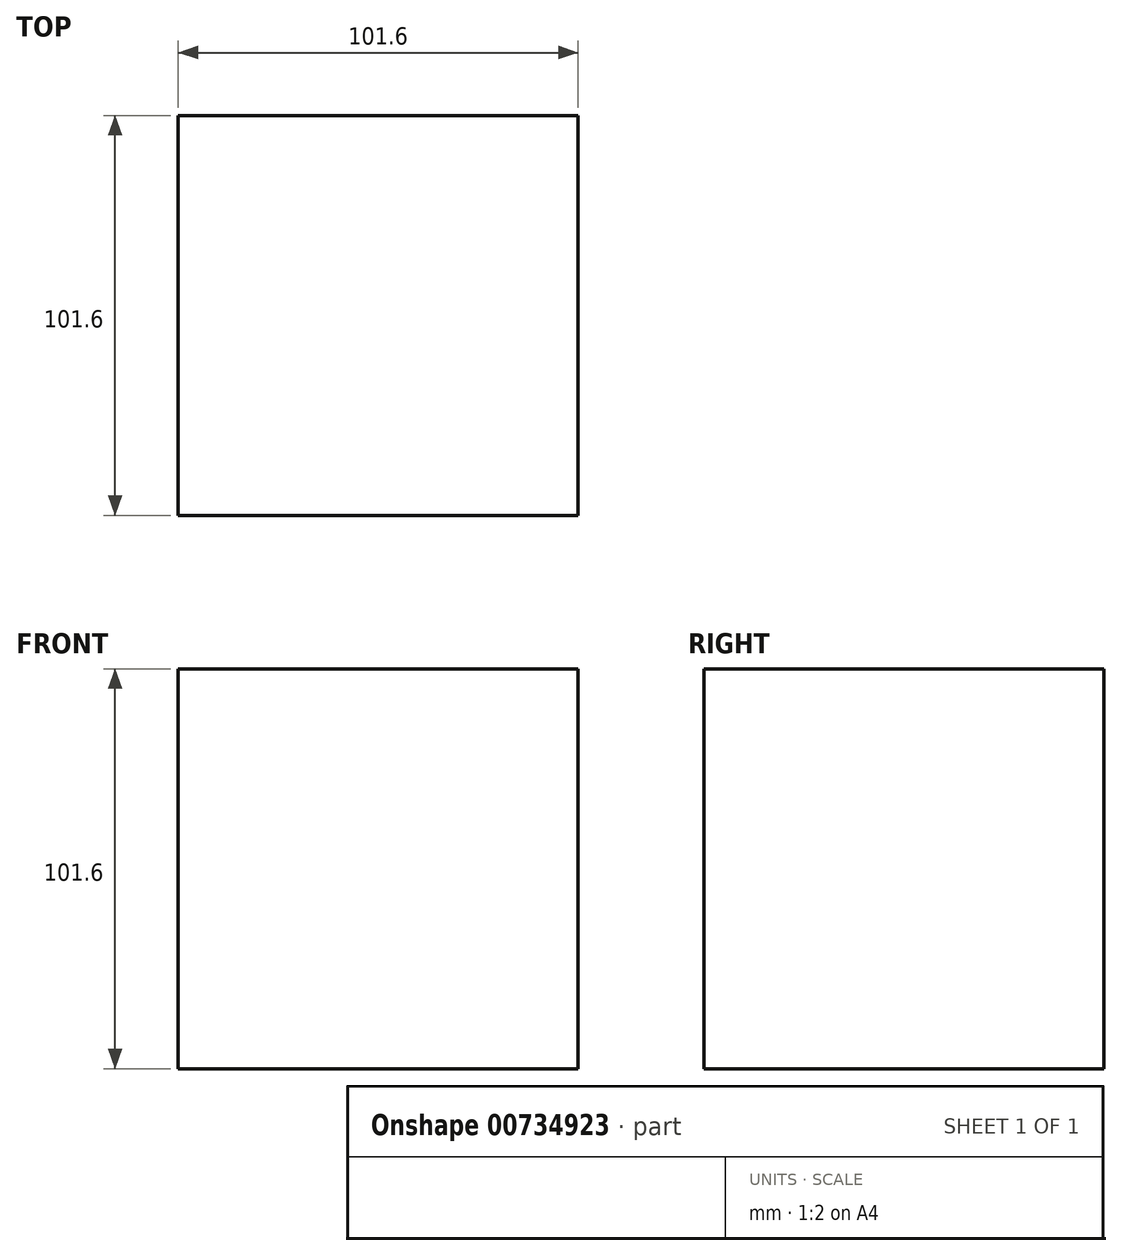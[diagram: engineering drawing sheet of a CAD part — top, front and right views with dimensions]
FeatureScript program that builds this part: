
annotation { "Feature Type Name" : "Feature", "Feature Type Description" : "" }
export const myFeature = defineFeature(function(context is Context, id is Id, definition is map)
    precondition{}
    {
        {
            var Q0;
            Q0=qCreatedBy(makeId("Top.planeOp"),FACE);
            var sketch = newSketch(context, id + "F0", { "sketchPlane" : qUnion([Q0])});
            skLineSegment(sketch, "E0.bottom", {"start": v(-51.63, 51.28) * mm, "end": v(49.97, 51.28) * mm});
            skLineSegment(sketch, "E0.top", {"start": v(-51.63, -50.32) * mm, "end": v(49.97, -50.32) * mm});
            skLineSegment(sketch, "E0.left", {"start": v(-51.63, 51.28) * mm, "end": v(-51.63, -50.32) * mm});
            skLineSegment(sketch, "E0.right", {"start": v(49.97, 51.28) * mm, "end": v(49.97, -50.32) * mm});
            skSolve(sketch);
        }
        {
            var Q0;
            Q0=makeQuery(id+"F0.imprint","IMPRINT",FACE,{"disambiguationData":[TD([[makeQuery(id+"F0.imprint","IMPRINT",EDGE,{"derivedFrom":sQuery(id+"F0.wireOp",EDGE,"E0.bottom")}),-1.0]])]});
            extrude(context, id + "F1", {"entities" : qUnion([Q0]), "depth" : 101.6 * mm, "offsetDistance" : 25.4 * mm});
        }
    });
